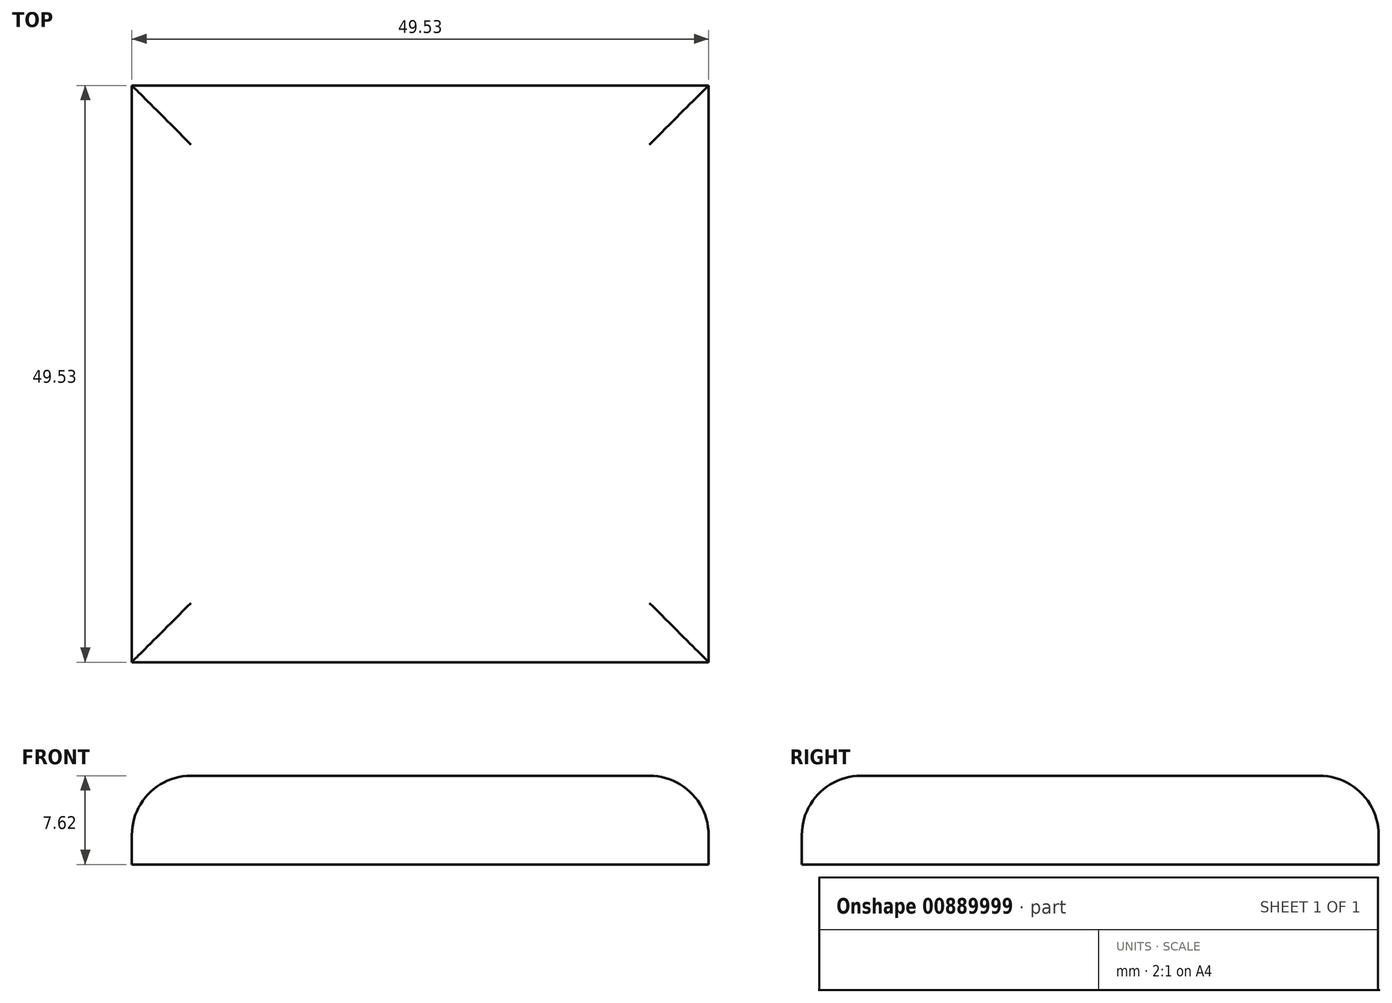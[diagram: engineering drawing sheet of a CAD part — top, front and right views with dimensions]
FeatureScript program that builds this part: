
annotation { "Feature Type Name" : "Feature", "Feature Type Description" : "" }
export const myFeature = defineFeature(function(context is Context, id is Id, definition is map)
    precondition{}
    {
        {
            var Q0;
            Q0=qCreatedBy(makeId("Top.planeOp"),FACE);
            var sketch = newSketch(context, id + "F0", { "sketchPlane" : qUnion([Q0])});
            skLineSegment(sketch, "E0.bottom", {"start": v(-21.75, 25.94) * mm, "end": v(27.78, 25.94) * mm});
            skLineSegment(sketch, "E0.top", {"start": v(-21.75, -23.6) * mm, "end": v(27.78, -23.6) * mm});
            skLineSegment(sketch, "E0.left", {"start": v(-21.75, 25.94) * mm, "end": v(-21.75, -23.6) * mm});
            skLineSegment(sketch, "E0.right", {"start": v(27.78, 25.94) * mm, "end": v(27.78, -23.6) * mm});
            skSolve(sketch);
        }
        {
            var Q0;
            Q0 = qSketchRegion(id + "F0", true);
            extrude(context, id + "F1", {"entities" : qUnion([Q0]), "depth" : 7.62 * mm, "offsetDistance" : 25.4 * mm});
        }
        {
            var Q0;
            Q0=makeQuery(id+"F1.opExtrude","CAP_EDGE",EDGE,{"disambiguationData":[OSD([sQuery(id+"F0.wireOp",EDGE,"E0.right")])],"isStart":false});
            var Q1;
            Q1=makeQuery(id+"F1.opExtrude","CAP_EDGE",EDGE,{"disambiguationData":[OSD([sQuery(id+"F0.wireOp",EDGE,"E0.top")])],"isStart":false});
            var Q2;
            Q2=makeQuery(id+"F1.opExtrude","CAP_EDGE",EDGE,{"disambiguationData":[OSD([sQuery(id+"F0.wireOp",EDGE,"E0.left")])],"isStart":false});
            var Q3;
            Q3=makeQuery(id+"F1.opExtrude","CAP_EDGE",EDGE,{"disambiguationData":[OSD([sQuery(id+"F0.wireOp",EDGE,"E0.bottom")])],"isStart":false});
            fillet(context, id + "F2", {"entities" : qUnion([Q0, Q1, Q2, Q3]), "radius" : 5.08 * mm, "tangentPropagation" : true, "allowEdgeOverflow" : false});
        }
    });
